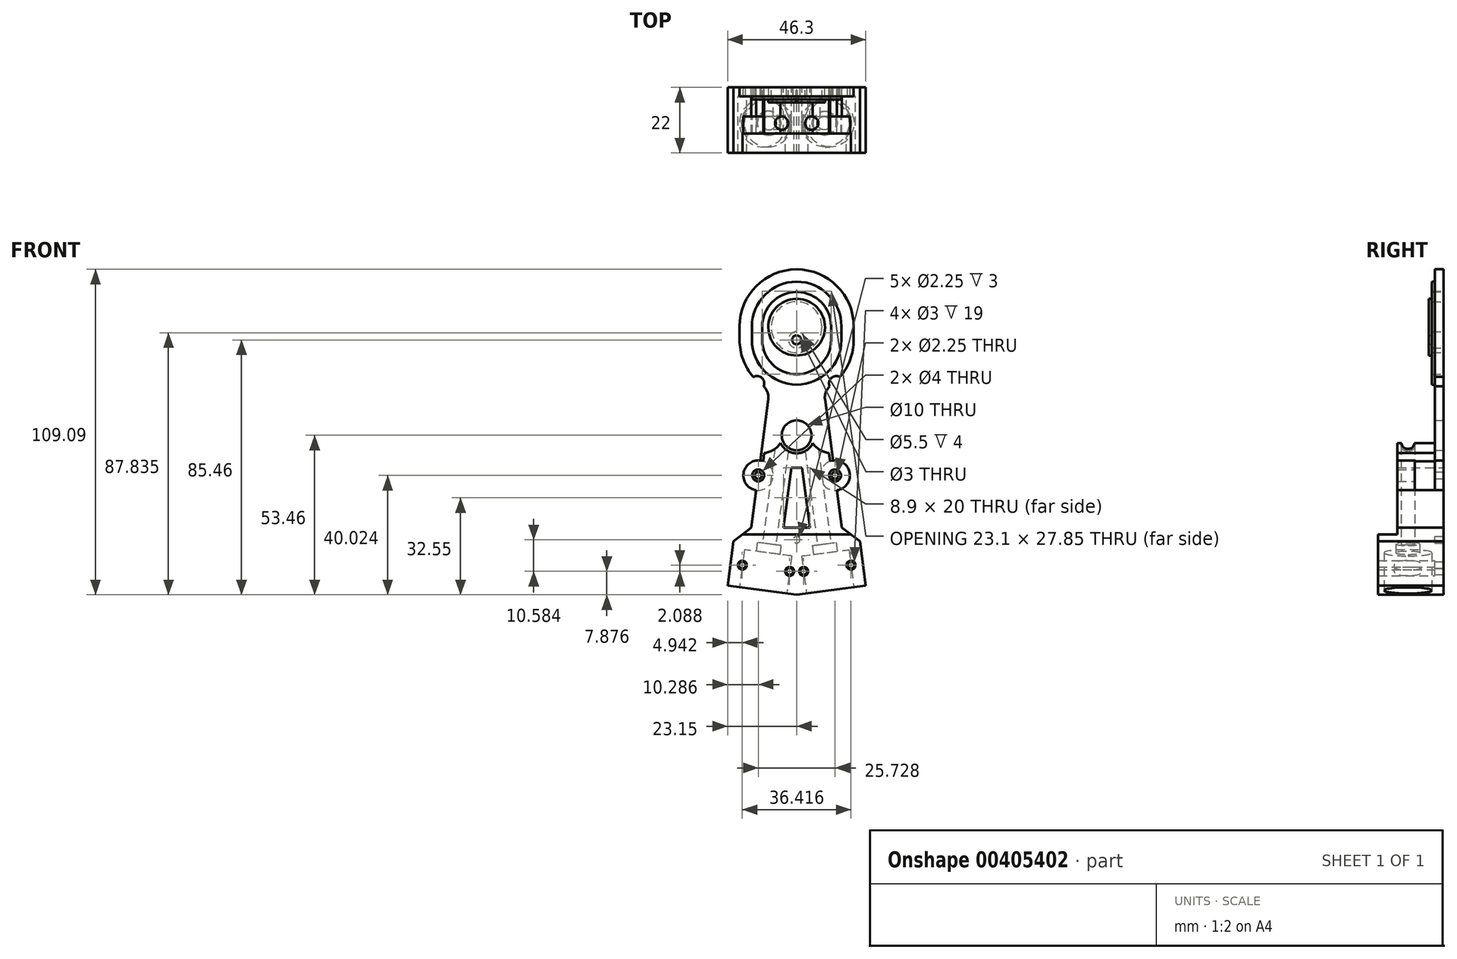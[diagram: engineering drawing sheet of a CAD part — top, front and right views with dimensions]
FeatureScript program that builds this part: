
annotation { "Feature Type Name" : "Feature", "Feature Type Description" : "" }
export const myFeature = defineFeature(function(context is Context, id is Id, definition is map)
    precondition{}
    {
        {
            var Q0;
            Q0=qCreatedBy(makeId("Front.planeOp"),FACE);
            var sketch = newSketch(context, id + "F0", { "sketchPlane" : qUnion([Q0])});
            skLineSegment(sketch, "E0", {"start": v(0, -53.46) * mm, "end": v(23.15, -50.4) * mm});
            skLineSegment(sketch, "E1", {"start": v(23.15, -50.4) * mm, "end": v(21.2, -35.54) * mm});
            skCircle(sketch, "E2", {"center": v(0, 0) * mm, "radius": 3.5 * mm, "construction": true});
            skLineSegment(sketch, "E3", {"start": v(2.47, 14.76) * mm, "end": v(11.26, -51.98) * mm, "construction": true});
            skLineSegment(sketch, "E4", {"start": v(0, -45.9) * mm, "end": v(22.17, -42.97) * mm, "construction": true});
            skCircle(sketch, "E5", {"center": v(2.34, -45.58) * mm, "radius": 1.5 * mm});
            skCircle(sketch, "E6", {"center": v(18.2, -43.5) * mm, "radius": 1.5 * mm});
            skLineSegment(sketch, "E7", {"start": v(0, 0) * mm, "end": v(20.43, 2.69) * mm, "construction": true});
            skCircle(sketch, "E8", {"center": v(12.86, -13.44) * mm, "radius": 2 * mm, "construction": true});
            skLineSegment(sketch, "E9", {"start": v(15.16, -30.91) * mm, "end": v(8.75, 17.85) * mm, "construction": true});
            skLineSegment(sketch, "E10", {"start": v(4.72, -38.91) * mm, "end": v(6.3, -50.97) * mm, "construction": true});
            skLineSegment(sketch, "E11", {"start": v(14.34, -38.66) * mm, "end": v(15.75, -49.38) * mm, "construction": true});
            skLineSegment(sketch, "E12", {"start": v(0, 41.33) * mm, "end": v(0, -57.6) * mm, "construction": true});
            skCircle(sketch, "E13", {"center": v(11.65, 1.53) * mm, "radius": 6.5 * mm, "construction": true});
            skLineSegment(sketch, "E14", {"start": v(1.68, 14.06) * mm, "end": v(5.3, -13.5) * mm});
            skLineSegment(sketch, "E15", {"start": v(3.46, 13.92) * mm, "end": v(7.07, -13.5) * mm});
            skCircle(sketch, "E16", {"center": v(-4.18, 31.73) * mm, "radius": 3 * mm, "construction": true});
            skLineSegment(sketch, "E17", {"start": v(0, 0) * mm, "end": v(-5.73, 43.53) * mm, "construction": true});
            skArc(sketch, "E18.trimOffspring", {"start": v(13.52, 29) * mm, "mid": v(-1.93, 31.94) * mm, "end": v(-16.92, 27.16) * mm, "construction": true});
            skCircle(sketch, "E19", {"center": v(0, 32) * mm, "radius": 3 * mm, "construction": true});
            skLineSegment(sketch, "E20", {"start": v(0, 0) * mm, "end": v(5.68, 43.17) * mm, "construction": true});
            skLineSegment(sketch, "E21", {"start": v(16.28, 32) * mm, "end": v(-17.99, 32) * mm, "construction": true});
            skPoint(sketch, "E22", {"position": v(4.21, 32) * mm});
            skCircle(sketch, "E23", {"center": v(-4.25, 32) * mm, "radius": 11.5 * mm, "construction": true});
            skPoint(sketch, "E24", {"position": v(-27.5, -31.5) * mm});
            skPoint(sketch, "E25", {"position": v(27.5, -31.5) * mm});
            skLineSegment(sketch, "E26", {"start": v(26.31, -34.75) * mm, "end": v(30.38, -49.9) * mm, "construction": true});
            skCircle(sketch, "E27", {"center": v(13.34, 17.39) * mm, "radius": 2 * mm, "construction": true});
            skLineSegment(sketch, "E28", {"start": v(0, 0) * mm, "end": v(17.13, 22.32) * mm, "construction": true});
            skLineSegment(sketch, "E29", {"start": v(0, 0) * mm, "end": v(20.92, 20.92) * mm, "construction": true});
            skCircle(sketch, "E30", {"center": v(15.5, 15.5) * mm, "radius": 2 * mm, "construction": true});
            skArc(sketch, "E31", {"start": v(19.32, 10.36) * mm, "mid": v(14.87, 16.1) * mm, "end": v(8.8, 20.07) * mm, "construction": true});
            skSolve(sketch);
        }
        {
            var Q0;
            Q0=qCreatedBy(makeId("Front.planeOp"),FACE);
            var sketch = newSketch(context, id + "F1", { "sketchPlane" : qUnion([Q0])});
            skLineSegment(sketch, "E32", {"start": v(0, -53.46) * mm, "end": v(23.15, -50.4) * mm});
            skLineSegment(sketch, "E33", {"start": v(0, 15.17) * mm, "end": v(9.1, 15.17) * mm});
            skArc(sketch, "E34", {"start": v(0, 5) * mm, "mid": v(5, 0) * mm, "end": v(0, -5) * mm});
            skLineSegment(sketch, "E35", {"start": v(23.15, -50.4) * mm, "end": v(21.2, -35.54) * mm});
            skLineSegment(sketch, "E36", {"start": v(15.16, -30.91) * mm, "end": v(21.2, -35.54) * mm});
            skLineSegment(sketch, "E37", {"start": v(15.16, -30.91) * mm, "end": v(13.52, -18.4) * mm});
            skLineSegment(sketch, "E38", {"start": v(0, 15.17) * mm, "end": v(0, -33.88) * mm, "construction": true});
            skCircle(sketch, "E39", {"center": v(0, 0) * mm, "radius": 3.5 * mm, "construction": true});
            skLineSegment(sketch, "E40", {"start": v(0, -45.9) * mm, "end": v(22.17, -42.97) * mm, "construction": true});
            skCircle(sketch, "E41", {"center": v(2.34, -45.58) * mm, "radius": 1.13 * mm});
            skCircle(sketch, "E42", {"center": v(18.2, -43.5) * mm, "radius": 1.13 * mm});
            skLineSegment(sketch, "E43", {"start": v(0, -30.91) * mm, "end": v(4.45, -30.91) * mm});
            skLineSegment(sketch, "E44", {"start": v(4.45, -30.91) * mm, "end": v(1.81, -10.91) * mm});
            skLineSegment(sketch, "E45", {"start": v(1.81, -10.91) * mm, "end": v(0, -10.91) * mm});
            skLineSegment(sketch, "E46", {"start": v(0, 0) * mm, "end": v(13.9, 1.83) * mm, "construction": true});
            skArc(sketch, "E47", {"start": v(13.52, -18.4) * mm, "mid": v(17.82, -12.78) * mm, "end": v(12.21, -8.48) * mm});
            skCircle(sketch, "E48", {"center": v(12.86, -13.44) * mm, "radius": 1.13 * mm});
            skLineSegment(sketch, "E49.trimOffspring", {"start": v(12.21, -8.48) * mm, "end": v(9.1, 15.17) * mm});
            skLineSegment(sketch, "E50", {"start": v(0, 0) * mm, "end": v(14.05, 0) * mm, "construction": true});
            skLineSegment(sketch, "E51", {"start": v(9.1, 15.17) * mm, "end": v(15.16, -30.91) * mm, "construction": true});
            skLineSegment(sketch, "E52", {"start": v(0, 15.17) * mm, "end": v(0, 5) * mm});
            skLineSegment(sketch, "E53", {"start": v(0, -5) * mm, "end": v(0, -10.91) * mm});
            skLineSegment(sketch, "E54", {"start": v(0, -30.91) * mm, "end": v(0, -33.88) * mm});
            skArc(sketch, "E55", {"start": v(0, -36.13) * mm, "mid": v(1.13, -35) * mm, "end": v(0, -33.88) * mm});
            skLineSegment(sketch, "E56.trimOffspring", {"start": v(0, -36.13) * mm, "end": v(0, -53.46) * mm, "construction": true});
            skLineSegment(sketch, "E57.trimOffspring", {"start": v(0, -36.13) * mm, "end": v(0, -53.46) * mm});
            skLineSegment(sketch, "E58", {"start": v(3.1, 10.01) * mm, "end": v(11.84, -56.4) * mm, "construction": true});
            skLineSegment(sketch, "E59", {"start": v(2.6, 7.02) * mm, "end": v(4.72, -9.07) * mm, "construction": true});
            skLineSegment(sketch, "E60", {"start": v(4.37, 7.02) * mm, "end": v(6.5, -9.07) * mm, "construction": true});
            skSolve(sketch);
        }
        {
            var Q0;
            Q0=qSketchRegion(id+"F1",true);
            extrude(context, id + "F2", {"entities" : qUnion([Q0]), "depth" : 3 * mm});
        }
        {
            var Q0;
            Q0=makeQuery(id+"F2.opExtrude","SWEPT_BODY",BODY,{"disambiguationData":[OSD([sQuery(id+"F1.wireOp",EDGE,"E32"),sQuery(id+"F1.wireOp",EDGE,"E33"),sQuery(id+"F1.wireOp",EDGE,"E34"),sQuery(id+"F1.wireOp",EDGE,"E35"),sQuery(id+"F1.wireOp",EDGE,"E36"),sQuery(id+"F1.wireOp",EDGE,"E37"),sQuery(id+"F1.wireOp",EDGE,"E41"),sQuery(id+"F1.wireOp",EDGE,"E42"),sQuery(id+"F1.wireOp",EDGE,"E43"),sQuery(id+"F1.wireOp",EDGE,"E44"),sQuery(id+"F1.wireOp",EDGE,"E45"),sQuery(id+"F1.wireOp",EDGE,"E47"),sQuery(id+"F1.wireOp",EDGE,"E48"),sQuery(id+"F1.wireOp",EDGE,"E49.trimOffspring"),sQuery(id+"F1.wireOp",EDGE,"E52"),sQuery(id+"F1.wireOp",EDGE,"E53"),sQuery(id+"F1.wireOp",EDGE,"E54")])]});
            var Q1;
            Q1=makeQuery(id+"F2.opExtrude","SWEPT_FACE",FACE,{"disambiguationData":[OSD([sQuery(id+"F1.wireOp",EDGE,"E52")])]});
            mirror(context, id + "F3", {"operationType" : NewBodyOperationType.ADD, "entities" : qUnion([Q0]), "mirrorPlane" : qUnion([Q1])});
        }
        {
            var Q0;
            Q0=qCreatedBy(makeId("Front.planeOp"),FACE);
            var sketch = newSketch(context, id + "F4", { "sketchPlane" : qUnion([Q0])});
            skLineSegment(sketch, "E61", {"start": v(14, 36.5) * mm, "end": v(14, 32) * mm});
            skLineSegment(sketch, "E62", {"start": v(-14, 36.5) * mm, "end": v(-14, 32) * mm});
            skArc(sketch, "E63", {"start": v(14, 36.5) * mm, "mid": v(0, 50.5) * mm, "end": v(-14, 36.5) * mm});
            skArc(sketch, "E64", {"start": v(-14, 32) * mm, "mid": v(0, 18) * mm, "end": v(14, 32) * mm});
            skArc(sketch, "E65", {"start": v(9.1, 15.17) * mm, "mid": v(10.1, 15.75) * mm, "end": v(11.05, 16.39) * mm});
            skArc(sketch, "E66", {"start": v(-19.13, 36.5) * mm, "mid": v(0, 55.63) * mm, "end": v(19.13, 36.5) * mm});
            skLineSegment(sketch, "E67", {"start": v(-19.13, 36.5) * mm, "end": v(-19.13, 32) * mm});
            skLineSegment(sketch, "E68", {"start": v(19.13, 36.5) * mm, "end": v(19.13, 32) * mm});
            skLineSegment(sketch, "E69", {"start": v(-9.1, 15.17) * mm, "end": v(9.1, 15.17) * mm});
            skArc(sketch, "E70.trimOffspring", {"start": v(-19.13, 32) * mm, "mid": v(-17.95, 25.38) * mm, "end": v(-14.55, 19.58) * mm});
            skArc(sketch, "E71", {"start": v(14.55, 19.58) * mm, "mid": v(11.66, 19.23) * mm, "end": v(11.05, 16.39) * mm});
            skArc(sketch, "E72.trimOffspring", {"start": v(14.55, 19.58) * mm, "mid": v(17.95, 25.38) * mm, "end": v(19.13, 32) * mm});
            skArc(sketch, "E73.MirrorCS", {"start": v(-14.55, 19.58) * mm, "mid": v(-11.66, 19.23) * mm, "end": v(-11.05, 16.39) * mm});
            skArc(sketch, "E74.trimOffspring", {"start": v(-11.05, 16.39) * mm, "mid": v(-10.1, 15.75) * mm, "end": v(-9.1, 15.17) * mm});
            skSolve(sketch);
        }
        {
            var Q0;
            Q0=qSketchRegion(id+"F4",true);
            extrude(context, id + "F5", {"entities" : qUnion([Q0]), "operationType" : NewBodyOperationType.ADD, "depth" : 3 * mm});
        }
        {
            var Q0;
            Q0=makeQuery(id+"F5.boolean.opBoolean","MERGE",EDGE,{"derivedFrom":[makeQuery(id+"F3.opPattern","COPY",EDGE,{"derivedFrom":makeQuery(id+"F2.opExtrude","SWEPT_EDGE",EDGE,{"disambiguationData":[OSD([sQuery(id+"F1.wireOp",EDGE,"E33"),sQuery(id+"F1.wireOp",EDGE,"E49.trimOffspring")])]}),"instanceName":"1"}),makeQuery(id+"F5.opExtrude","SWEPT_EDGE",EDGE,{"disambiguationData":[OSD([sQuery(id+"F4.wireOp",EDGE,"E69"),sQuery(id+"F4.wireOp",EDGE,"E74.trimOffspring")])]})]});
            var Q1;
            Q1=makeQuery(id+"F5.boolean.opBoolean","MERGE",EDGE,{"derivedFrom":[makeQuery(id+"F2.opExtrude","SWEPT_EDGE",EDGE,{"disambiguationData":[OSD([sQuery(id+"F1.wireOp",EDGE,"E33"),sQuery(id+"F1.wireOp",EDGE,"E49.trimOffspring")])]}),makeQuery(id+"F5.opExtrude","SWEPT_EDGE",EDGE,{"disambiguationData":[OSD([sQuery(id+"F4.wireOp",EDGE,"E65"),sQuery(id+"F4.wireOp",EDGE,"E69")])]})]});
            fillet(context, id + "F6", {"entities" : qUnion([Q0, Q1]), "radius" : 5 * mm, "tangentPropagation" : true, "allowEdgeOverflow" : false});
        }
        {
            var Q0;
            {var subQ0=makeQuery(id+"F2.opExtrude","CAP_FACE",FACE,{"disambiguationData":[OSD([sQuery(id+"F1.wireOp",EDGE,"E32"),sQuery(id+"F1.wireOp",EDGE,"E33"),sQuery(id+"F1.wireOp",EDGE,"E34"),sQuery(id+"F1.wireOp",EDGE,"E35"),sQuery(id+"F1.wireOp",EDGE,"E36"),sQuery(id+"F1.wireOp",EDGE,"E37"),sQuery(id+"F1.wireOp",EDGE,"E41"),sQuery(id+"F1.wireOp",EDGE,"E42"),sQuery(id+"F1.wireOp",EDGE,"E43"),sQuery(id+"F1.wireOp",EDGE,"E44"),sQuery(id+"F1.wireOp",EDGE,"E45"),sQuery(id+"F1.wireOp",EDGE,"E47"),sQuery(id+"F1.wireOp",EDGE,"E48"),sQuery(id+"F1.wireOp",EDGE,"E49.trimOffspring"),sQuery(id+"F1.wireOp",EDGE,"E52"),sQuery(id+"F1.wireOp",EDGE,"E53"),sQuery(id+"F1.wireOp",EDGE,"E54"),sQuery(id+"F1.wireOp",EDGE,"E55"),sQuery(id+"F1.wireOp",EDGE,"E57.trimOffspring")])],"isStart":false});Q0=makeQuery(id+"F5.boolean.opBoolean","MERGE",FACE,{"derivedFrom":[makeQuery(id+"F3.boolean.opBoolean","MERGE",FACE,{"derivedFrom":[subQ0,makeQuery(id+"F3.opPattern","COPY",FACE,{"derivedFrom":subQ0,"instanceName":"1"})]}),makeQuery(id+"F5.opExtrude","CAP_FACE",FACE,{"disambiguationData":[OSD([sQuery(id+"F4.wireOp",EDGE,"XSR0kVj8-n9yJ-rhlM-9lze-rqYWqVYd3YQn"),sQuery(id+"F4.wireOp",EDGE,"zioKGPXW-v3R5-f5bc-qALi-ecG3NecYjB9o"),sQuery(id+"F4.wireOp",EDGE,"iLwt3fKu-8mGT-0oiL-bdYg-F2hBGaAt47RT"),sQuery(id+"F4.wireOp",EDGE,"XHtRUne4-3xnD-M1Hv-dgk4-vEHfuz4qDRqg"),sQuery(id+"F4.wireOp",EDGE,"E61"),sQuery(id+"F4.wireOp",EDGE,"E62"),sQuery(id+"F4.wireOp",EDGE,"E63"),sQuery(id+"F4.wireOp",EDGE,"E64"),sQuery(id+"F4.wireOp",EDGE,"Vgy9tToT-xj2W-KrKx-thH2-jMpY4nkcRg8E"),sQuery(id+"F4.wireOp",EDGE,"UzgCGOXo-iD4m-cqxA-ZLwE-A7n1dnBs3Ghd")])],"isStart":false})]});}
            var sketch = newSketch(context, id + "F7", { "sketchPlane" : qUnion([Q0])});
            skLineSegment(sketch, "E75", {"start": v(0, -53.46) * mm, "end": v(23.15, -50.4) * mm});
            skLineSegment(sketch, "E76", {"start": v(23.15, -50.4) * mm, "end": v(21.2, -35.54) * mm});
            skLineSegment(sketch, "E77", {"start": v(15.16, -30.91) * mm, "end": v(21.2, -35.54) * mm});
            skLineSegment(sketch, "E78", {"start": v(15.16, -30.91) * mm, "end": v(13.52, -18.4) * mm});
            skCircle(sketch, "E79", {"center": v(0, 0) * mm, "radius": 3.5 * mm, "construction": true});
            skLineSegment(sketch, "E80", {"start": v(0, -45.9) * mm, "end": v(22.17, -42.97) * mm, "construction": true});
            skCircle(sketch, "E81", {"center": v(2.34, -45.58) * mm, "radius": 1.5 * mm});
            skCircle(sketch, "E82", {"center": v(18.2, -43.5) * mm, "radius": 1.5 * mm});
            skLineSegment(sketch, "E83.trimOffspring", {"start": v(0, -6) * mm, "end": v(0, -10.91) * mm});
            skLineSegment(sketch, "E84", {"start": v(0, -30.91) * mm, "end": v(4.45, -30.91) * mm});
            skLineSegment(sketch, "E85", {"start": v(4.45, -30.91) * mm, "end": v(1.81, -10.91) * mm});
            skLineSegment(sketch, "E86", {"start": v(1.81, -10.91) * mm, "end": v(0, -10.91) * mm});
            skLineSegment(sketch, "E87.trimOffspring", {"start": v(0, -30.91) * mm, "end": v(0, -53.46) * mm});
            skLineSegment(sketch, "E88", {"start": v(0, 0) * mm, "end": v(16.5, 2.17) * mm, "construction": true});
            skArc(sketch, "E89", {"start": v(13.52, -18.4) * mm, "mid": v(17.82, -12.78) * mm, "end": v(12.21, -8.48) * mm});
            skCircle(sketch, "E90", {"center": v(12.86, -13.44) * mm, "radius": 2 * mm});
            skLineSegment(sketch, "E91", {"start": v(10.87, -5.93) * mm, "end": v(11.22, -8.6) * mm});
            skLineSegment(sketch, "E92", {"start": v(11.22, -8.6) * mm, "end": v(12.21, -8.48) * mm});
            skLineSegment(sketch, "E93", {"start": v(15.16, -30.91) * mm, "end": v(8.83, 17.22) * mm, "construction": true});
            skLineSegment(sketch, "E94", {"start": v(1.76, 20.12) * mm, "end": v(12.02, -57.8) * mm, "construction": true});
            skLineSegment(sketch, "E95", {"start": v(2.13, 10.64) * mm, "end": v(5.17, -12.49) * mm, "construction": true});
            skLineSegment(sketch, "E96", {"start": v(3.9, 10.64) * mm, "end": v(6.94, -12.49) * mm, "construction": true});
            skArc(sketch, "E97.trimOffspring", {"start": v(5.4, -2.61) * mm, "mid": v(3.19, -5.08) * mm, "end": v(0, -6) * mm});
            skArc(sketch, "E98", {"start": v(5.4, -2.61) * mm, "mid": v(8.2, -5.13) * mm, "end": v(11.88, -5.96) * mm});
            skLineSegment(sketch, "E99", {"start": v(23.9, -56.1) * mm, "end": v(17.06, -4.12) * mm, "construction": true});
            skSolve(sketch);
        }
        {
            var Q0;
            Q0=qSketchRegion(id+"F7",true);
            extrude(context, id + "F8", {"entities" : qUnion([Q0]), "depth" : 19 * mm});
        }
        {
            var Q0;
            Q0=makeQuery(id+"F8.opExtrude","CAP_FACE",FACE,{"disambiguationData":[OSD([sQuery(id+"F7.wireOp",EDGE,"E75"),sQuery(id+"F7.wireOp",EDGE,"2674ecda-7bdb-4b88-ab8f-22eb12c7f57d"),sQuery(id+"F7.wireOp",EDGE,"daed260d-e0ce-475e-a80a-172ad7bc1b56"),sQuery(id+"F7.wireOp",EDGE,"E76"),sQuery(id+"F7.wireOp",EDGE,"E77"),sQuery(id+"F7.wireOp",EDGE,"E78"),sQuery(id+"F7.wireOp",EDGE,"d0cc75f4-926d-4b6a-8d15-d4eb5ab97802"),sQuery(id+"F7.wireOp",EDGE,"E81"),sQuery(id+"F7.wireOp",EDGE,"E82"),sQuery(id+"F7.wireOp",EDGE,"E83.trimOffspring")])],"isStart":false});
            var sketch = newSketch(context, id + "F9", { "sketchPlane" : qUnion([Q0])});
            skLineSegment(sketch, "E100.left", {"start": v(0, -33.08) * mm, "end": v(0, -30.91) * mm});
            skLineSegment(sketch, "E101", {"start": v(0, -33.08) * mm, "end": v(0, -33.22) * mm});
            skLineSegment(sketch, "E102", {"start": v(0, -33.22) * mm, "end": v(18.18, -33.22) * mm});
            skLineSegment(sketch, "E103", {"start": v(13.52, -18.4) * mm, "end": v(15.3, -31.9) * mm});
            skLineSegment(sketch, "E104", {"start": v(13.52, -18.4) * mm, "end": v(13.52, -18.4) * mm});
            skLineSegment(sketch, "E105", {"start": v(10.87, -5.93) * mm, "end": v(11.22, -8.6) * mm});
            skLineSegment(sketch, "E106", {"start": v(11.22, -8.6) * mm, "end": v(12.21, -8.48) * mm});
            skArc(sketch, "E107", {"start": v(13.52, -18.4) * mm, "mid": v(17.82, -12.78) * mm, "end": v(12.21, -8.48) * mm});
            skPoint(sketch, "E108.start.orphan", {"position": v(3.19, -5.08) * mm});
            skLineSegment(sketch, "E109", {"start": v(15.16, -30.91) * mm, "end": v(18.18, -33.22) * mm});
            skLineSegment(sketch, "E110", {"start": v(0, -10.91) * mm, "end": v(1.81, -10.91) * mm});
            skLineSegment(sketch, "E111", {"start": v(1.81, -10.91) * mm, "end": v(4.45, -30.91) * mm});
            skLineSegment(sketch, "E112", {"start": v(4.45, -30.91) * mm, "end": v(0, -30.91) * mm});
            skLineSegment(sketch, "E113.trimOffspring", {"start": v(0, -10.91) * mm, "end": v(0, -6) * mm});
            skArc(sketch, "E114", {"start": v(2.2, -5.59) * mm, "mid": v(2.7, -5.36) * mm, "end": v(3.19, -5.08) * mm});
            skArc(sketch, "E115", {"start": v(7.35, -4.6) * mm, "mid": v(19.37, 4.7) * mm, "end": v(4.17, 4.32) * mm});
            skSolve(sketch);
        }
        {
            var Q0;
            {var subQ4=sQuery(id+"F9.wireOp",EDGE,"E103");Q0=makeQuery(id+"F9.imprint","IMPRINT",FACE,{"disambiguationData":[TD([[makeQuery(id+"F9.imprint","IMPRINT",EDGE,{"derivedFrom":subQ4}),1.0]])]});}
            extrude(context, id + "F10", {"entities" : qUnion([Q0]), "operationType" : NewBodyOperationType.REMOVE, "oppositeDirection" : true, "depth" : 6.5 * mm});
        }
        {
            var Q0;
            {var subQ0=makeQuery(id+"F2.opExtrude","CAP_FACE",FACE,{"disambiguationData":[OSD([sQuery(id+"F1.wireOp",EDGE,"E32"),sQuery(id+"F1.wireOp",EDGE,"E33"),sQuery(id+"F1.wireOp",EDGE,"E34"),sQuery(id+"F1.wireOp",EDGE,"E35"),sQuery(id+"F1.wireOp",EDGE,"E36"),sQuery(id+"F1.wireOp",EDGE,"E37"),sQuery(id+"F1.wireOp",EDGE,"E41"),sQuery(id+"F1.wireOp",EDGE,"E42"),sQuery(id+"F1.wireOp",EDGE,"E43"),sQuery(id+"F1.wireOp",EDGE,"E44"),sQuery(id+"F1.wireOp",EDGE,"E45"),sQuery(id+"F1.wireOp",EDGE,"E47"),sQuery(id+"F1.wireOp",EDGE,"E48"),sQuery(id+"F1.wireOp",EDGE,"E49.trimOffspring"),sQuery(id+"F1.wireOp",EDGE,"E52"),sQuery(id+"F1.wireOp",EDGE,"E53"),sQuery(id+"F1.wireOp",EDGE,"E54"),sQuery(id+"F1.wireOp",EDGE,"E55"),sQuery(id+"F1.wireOp",EDGE,"E57.trimOffspring")])],"isStart":false});Q0=makeQuery(id+"F3.boolean.opBoolean","MERGE",FACE,{"derivedFrom":[subQ0,makeQuery(id+"F3.opPattern","COPY",FACE,{"derivedFrom":subQ0,"instanceName":"1"})]});}
            var sketch = newSketch(context, id + "F11", { "sketchPlane" : qUnion([Q0])});
            skCircle(sketch, "E116.converted", {"center": v(12.86, -13.44) * mm, "radius": 5 * mm});
            skLineSegment(sketch, "E117", {"start": v(12.21, -8.48) * mm, "end": v(11.22, -8.6) * mm});
            skLineSegment(sketch, "E118", {"start": v(11.22, -8.6) * mm, "end": v(11.23, -8.7) * mm});
            skSolve(sketch);
        }
        {
            var Q0;
            Q0=qSketchRegion(id+"F11",true);
            extrude(context, id + "F12", {"entities" : qUnion([Q0]), "operationType" : NewBodyOperationType.REMOVE, "depth" : 6.75 * mm});
        }
        {
            var Q0;
            Q0=makeQuery(id+"F8.opExtrude","SWEPT_FACE",FACE,{"disambiguationData":[OSD([sQuery(id+"F7.wireOp",EDGE,"E75")])]});
            var sketch = newSketch(context, id + "F13", { "sketchPlane" : qUnion([Q0])});
            skCircle(sketch, "E119", {"center": v(4.37, 12) * mm, "radius": 8 * mm});
            skSolve(sketch);
        }
        {
            var Q0;
            Q0=qSketchRegion(id+"F13",true);
            extrude(context, id + "F14", {"entities" : qUnion([Q0]), "operationType" : NewBodyOperationType.REMOVE, "oppositeDirection" : true, "depth" : 12.7 * mm});
        }
        {
            var Q0;
            Q0=makeQuery(id+"F14.boolean.opBoolean","COPY",FACE,{"derivedFrom":makeQuery(id+"F14.opExtrude","CAP_FACE",FACE,{"disambiguationData":[OSD([sQuery(id+"F13.wireOp",EDGE,"E119")])],"isStart":false})});
            var sketch = newSketch(context, id + "F15", { "sketchPlane" : qUnion([Q0])});
            skCircle(sketch, "E120", {"center": v(4.37, 12) * mm, "radius": 4 * mm});
            skSolve(sketch);
        }
        {
            var Q0;
            Q0=qSketchRegion(id+"F15",true);
            extrude(context, id + "F16", {"entities" : qUnion([Q0]), "operationType" : NewBodyOperationType.REMOVE, "oppositeDirection" : true, "depth" : 3 * mm});
        }
        {
            var Q0;
            Q0=makeQuery(id+"F16.boolean.opBoolean","COPY",FACE,{"derivedFrom":makeQuery(id+"F16.opExtrude","CAP_FACE",FACE,{"disambiguationData":[OSD([sQuery(id+"F15.wireOp",EDGE,"E120")])],"isStart":false})});
            var sketch = newSketch(context, id + "F17", { "sketchPlane" : qUnion([Q0])});
            skCircle(sketch, "E121", {"center": v(4.37, 12) * mm, "radius": 2.25 * mm});
            skSolve(sketch);
        }
        {
            var Q0;
            Q0=qSketchRegion(id+"F17",true);
            extrude(context, id + "F18", {"entities" : qUnion([Q0]), "operationType" : NewBodyOperationType.REMOVE, "endBound" : BoundingType.THROUGH_ALL, "oppositeDirection" : true, "depth" : 25 * mm});
        }
        {
            var Q0;
            Q0=makeQuery(id+"F8.opExtrude","SWEPT_BODY",BODY,{"disambiguationData":[OSD([sQuery(id+"F7.wireOp",EDGE,"E75"),sQuery(id+"F7.wireOp",EDGE,"2674ecda-7bdb-4b88-ab8f-22eb12c7f57d"),sQuery(id+"F7.wireOp",EDGE,"daed260d-e0ce-475e-a80a-172ad7bc1b56"),sQuery(id+"F7.wireOp",EDGE,"E76"),sQuery(id+"F7.wireOp",EDGE,"E77"),sQuery(id+"F7.wireOp",EDGE,"E78"),sQuery(id+"F7.wireOp",EDGE,"d0cc75f4-926d-4b6a-8d15-d4eb5ab97802"),sQuery(id+"F7.wireOp",EDGE,"E81"),sQuery(id+"F7.wireOp",EDGE,"E82"),sQuery(id+"F7.wireOp",EDGE,"E83.trimOffspring")])]});
            var Q1;
            Q1=makeQuery(id+"F8.opExtrude","SWEPT_FACE",FACE,{"disambiguationData":[OSD([sQuery(id+"F7.wireOp",EDGE,"E83.trimOffspring")])]});
            mirror(context, id + "F19", {"operationType" : NewBodyOperationType.ADD, "entities" : qUnion([Q0]), "mirrorPlane" : qUnion([Q1])});
        }
        {
            var Q0;
            Q0=qCreatedBy(makeId("Front.planeOp"),FACE);
            var sketch = newSketch(context, id + "F20", { "sketchPlane" : qUnion([Q0])});
            skCircle(sketch, "E122", {"center": v(0, 32) * mm, "radius": 2.75 * mm});
            skCircle(sketch, "E123.converted", {"center": v(0, 36.25) * mm, "radius": 8.5 * mm});
            skSolve(sketch);
        }
        {
            var Q0;
            Q0=qSketchRegion(id+"F20",true);
            extrude(context, id + "F21", {"entities" : qUnion([Q0]), "depth" : 4 * mm});
        }
        {
            var Q0;
            Q0=makeQuery(id+"F21.opExtrude","CAP_FACE",FACE,{"disambiguationData":[OSD([sQuery(id+"F20.wireOp",EDGE,"E122"),sQuery(id+"F20.wireOp",EDGE,"0a06fa43-1b5e-494f-aafe-d3341a653f43")])],"isStart":false});
            var sketch = newSketch(context, id + "F22", { "sketchPlane" : qUnion([Q0])});
            skArc(sketch, "E124", {"start": v(-0.25, 45.75) * mm, "mid": v(0, 26.75) * mm, "end": v(0.25, 45.75) * mm});
            skCircle(sketch, "E125", {"center": v(0, 32) * mm, "radius": 1.5 * mm});
            skArc(sketch, "E126", {"start": v(-0.25, 45.75) * mm, "mid": v(0, 45.5) * mm, "end": v(0.25, 45.75) * mm});
            skSolve(sketch);
        }
        {
            var Q0;
            Q0=qSketchRegion(id+"F22",true);
            extrude(context, id + "F23", {"entities" : qUnion([Q0]), "operationType" : NewBodyOperationType.ADD, "depth" : 1 * mm});
        }
        {
            var Q0;
            Q0=qCreatedBy(makeId("Front.planeOp"),FACE);
            var sketch = newSketch(context, id + "F24", { "sketchPlane" : qUnion([Q0])});
            skLineSegment(sketch, "E127", {"start": v(11.55, 36.5) * mm, "end": v(11.55, 32) * mm});
            skLineSegment(sketch, "E128", {"start": v(-11.55, 36.5) * mm, "end": v(-11.55, 32) * mm});
            skArc(sketch, "E129", {"start": v(11.55, 36.5) * mm, "mid": v(8.25, 44.58) * mm, "end": v(0.25, 48.05) * mm});
            skArc(sketch, "E130", {"start": v(-11.55, 32) * mm, "mid": v(0, 20.45) * mm, "end": v(11.55, 32) * mm});
            skArc(sketch, "E131", {"start": v(-14, 32) * mm, "mid": v(0, 18) * mm, "end": v(14, 32) * mm});
            skLineSegment(sketch, "E132", {"start": v(14, 36.5) * mm, "end": v(14, 32) * mm});
            skLineSegment(sketch, "E133", {"start": v(-14, 36.5) * mm, "end": v(-14, 32) * mm});
            skArc(sketch, "E134.trimOffspring", {"start": v(14, 36.5) * mm, "mid": v(0, 50.5) * mm, "end": v(-14, 36.5) * mm});
            skArc(sketch, "E135", {"start": v(0.25, 48.05) * mm, "mid": v(0, 48.3) * mm, "end": v(-0.25, 48.05) * mm});
            skArc(sketch, "E136.trimOffspring", {"start": v(-0.25, 48.05) * mm, "mid": v(-8.25, 44.58) * mm, "end": v(-11.55, 36.5) * mm});
            skSolve(sketch);
        }
        {
            var Q0;
            Q0=qSketchRegion(id+"F24",true);
            extrude(context, id + "F25", {"entities" : qUnion([Q0]), "depth" : 3 * mm});
        }
        {
            var Q0;
            Q0=makeQuery(id+"F25.opExtrude","CAP_FACE",FACE,{"disambiguationData":[OSD([sQuery(id+"F24.wireOp",EDGE,"E127"),sQuery(id+"F24.wireOp",EDGE,"E128"),sQuery(id+"F24.wireOp",EDGE,"E129"),sQuery(id+"F24.wireOp",EDGE,"E130"),sQuery(id+"F24.wireOp",EDGE,"E131"),sQuery(id+"F24.wireOp",EDGE,"E132"),sQuery(id+"F24.wireOp",EDGE,"E133"),sQuery(id+"F24.wireOp",EDGE,"E134.trimOffspring"),sQuery(id+"F24.wireOp",EDGE,"E135"),sQuery(id+"F24.wireOp",EDGE,"E136.trimOffspring")])],"isStart":false});
            var sketch = newSketch(context, id + "F26", { "sketchPlane" : qUnion([Q0])});
            skLineSegment(sketch, "E137", {"start": v(11.55, 36.5) * mm, "end": v(11.55, 32) * mm});
            skLineSegment(sketch, "E138", {"start": v(-11.55, 36.5) * mm, "end": v(-11.55, 32) * mm});
            skArc(sketch, "E139", {"start": v(11.55, 36.5) * mm, "mid": v(8.25, 44.58) * mm, "end": v(0.25, 48.05) * mm});
            skArc(sketch, "E140", {"start": v(-11.55, 32) * mm, "mid": v(0, 20.45) * mm, "end": v(11.55, 32) * mm});
            skArc(sketch, "E141", {"start": v(-15, 32) * mm, "mid": v(0, 17) * mm, "end": v(15, 32) * mm});
            skLineSegment(sketch, "E142", {"start": v(15, 36.5) * mm, "end": v(15, 32) * mm});
            skLineSegment(sketch, "E143", {"start": v(-15, 36.5) * mm, "end": v(-15, 32) * mm});
            skArc(sketch, "E144.trimOffspring", {"start": v(15, 36.5) * mm, "mid": v(0, 51.5) * mm, "end": v(-15, 36.5) * mm});
            skArc(sketch, "E145", {"start": v(0.25, 48.05) * mm, "mid": v(0, 48.3) * mm, "end": v(-0.25, 48.05) * mm});
            skArc(sketch, "E146.trimOffspring", {"start": v(-0.25, 48.05) * mm, "mid": v(-8.25, 44.58) * mm, "end": v(-11.55, 36.5) * mm});
            skSolve(sketch);
        }
        {
            var Q0;
            Q0=qSketchRegion(id+"F26",true);
            extrude(context, id + "F27", {"entities" : qUnion([Q0]), "operationType" : NewBodyOperationType.ADD, "depth" : 1 * mm});
        }
    });
